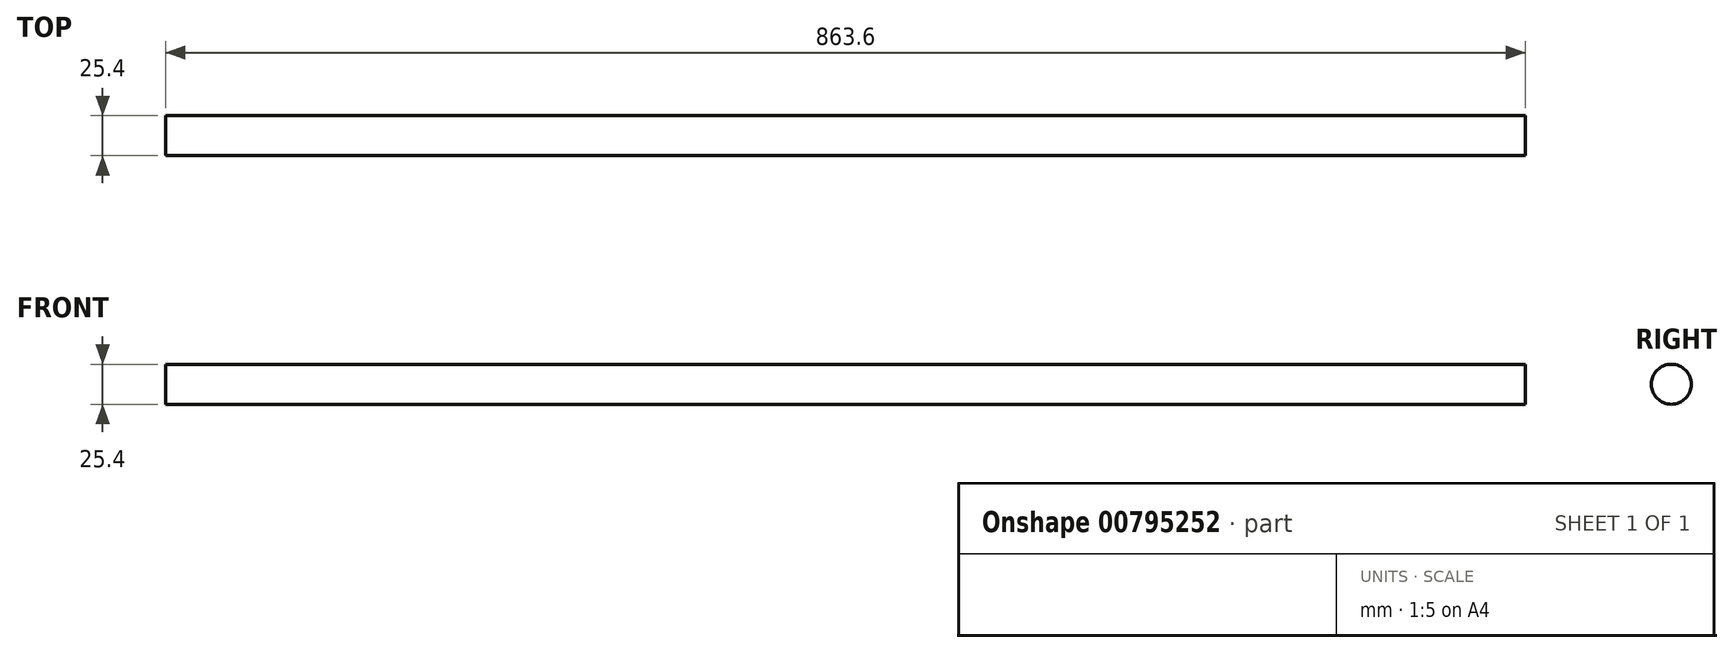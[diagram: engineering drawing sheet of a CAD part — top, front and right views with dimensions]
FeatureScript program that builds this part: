
annotation { "Feature Type Name" : "Feature", "Feature Type Description" : "" }
export const myFeature = defineFeature(function(context is Context, id is Id, definition is map)
    precondition{}
    {
        {
            var Q0;
            Q0=qCreatedBy(makeId("Right.planeOp"),FACE);
            var sketch = newSketch(context, id + "F0", { "sketchPlane" : qUnion([Q0])});
            skCircle(sketch, "E0", {"center": v(0, 0) * mm, "radius": 12.7 * mm});
            skSolve(sketch);
        }
        {
            var Q0;
            Q0=makeQuery(id+"F0.imprint","IMPRINT",FACE,{"disambiguationData":[TD([[makeQuery(id+"F0.imprint","IMPRINT",EDGE,{"derivedFrom":sQuery(id+"F0.wireOp",EDGE,"E0")}),1.0]])]});
            extrude(context, id + "F1", {"entities" : qUnion([Q0]), "depth" : 863.6 * mm, "offsetDistance" : 25.4 * mm, "symmetric" : true});
        }
    });
